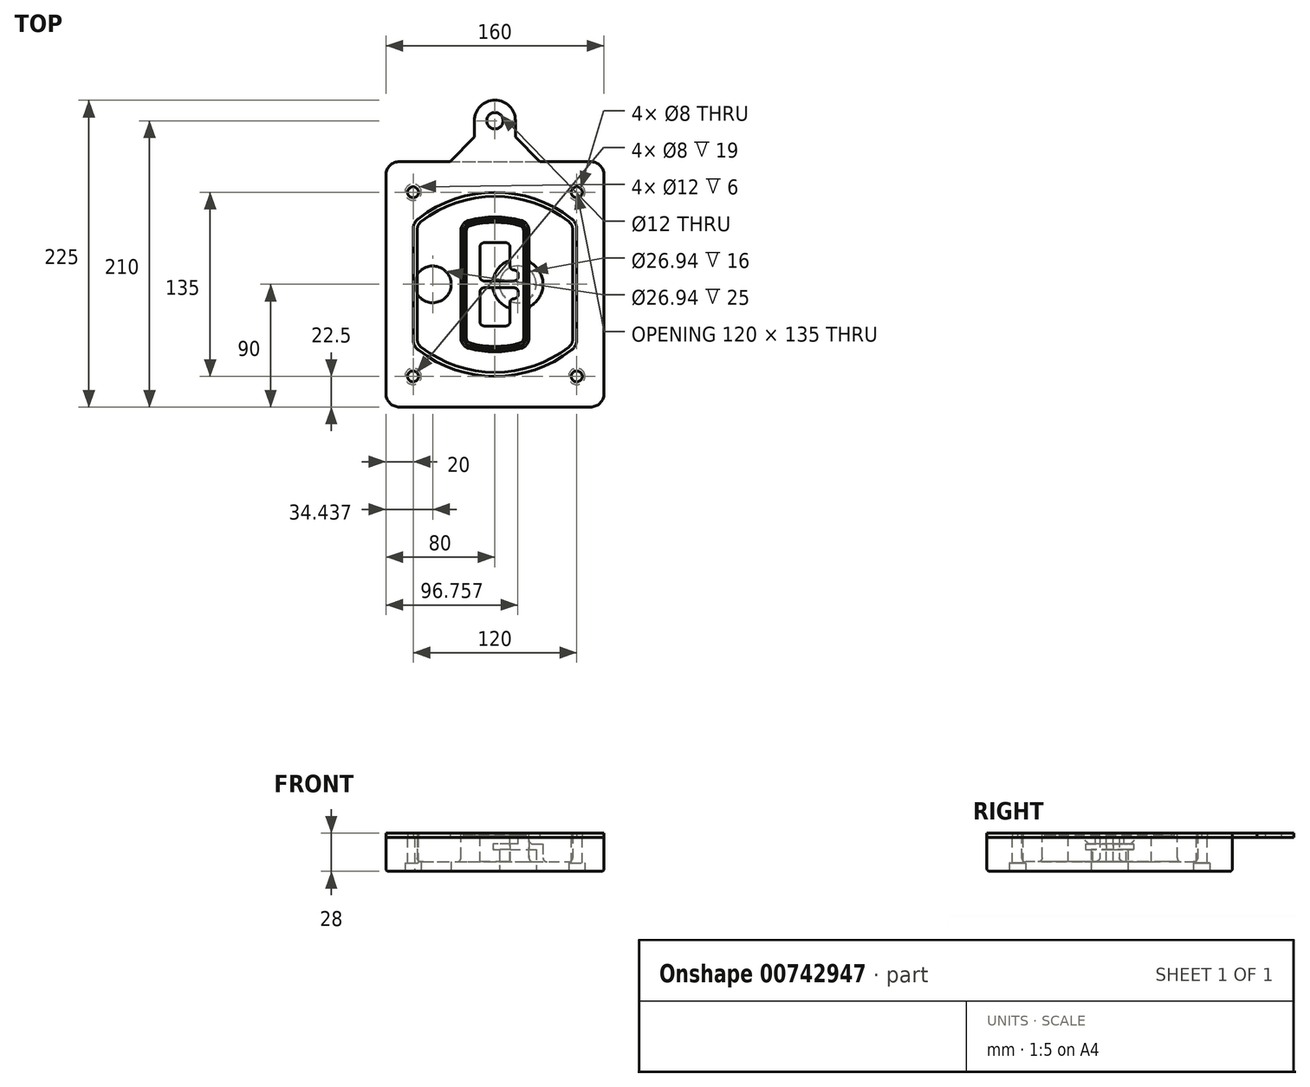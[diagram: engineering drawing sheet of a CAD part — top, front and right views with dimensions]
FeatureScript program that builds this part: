
annotation { "Feature Type Name" : "Feature", "Feature Type Description" : "" }
export const myFeature = defineFeature(function(context is Context, id is Id, definition is map)
    precondition{}
    {
        {
            var Q0;
            Q0=qCreatedBy(makeId("Top.planeOp"),FACE);
            var sketch = newSketch(context, id + "F0", { "sketchPlane" : qUnion([Q0])});
            skPoint(sketch, "E0.rect.middle", {"position": v(0, 0) * mm});
            skLineSegment(sketch, "E1.bottom", {"start": v(-70, -90) * mm, "end": v(70, -90) * mm});
            skLineSegment(sketch, "E1.top", {"start": v(-70, 90) * mm, "end": v(70, 90) * mm});
            skLineSegment(sketch, "E1.left", {"start": v(-80, -80) * mm, "end": v(-80, 80) * mm});
            skLineSegment(sketch, "E1.right", {"start": v(80, -80) * mm, "end": v(80, 80) * mm});
            skLineSegment(sketch, "E2", {"start": v(-80, 90) * mm, "end": v(80, -90) * mm, "construction": true});
            skLineSegment(sketch, "E3", {"start": v(80, 90) * mm, "end": v(-80, -90) * mm, "construction": true});
            skCircle(sketch, "E4", {"center": v(-60, 67.5) * mm, "radius": 4 * mm});
            skCircle(sketch, "E5", {"center": v(60, 67.5) * mm, "radius": 4 * mm});
            skCircle(sketch, "E6", {"center": v(60, -67.5) * mm, "radius": 4 * mm});
            skCircle(sketch, "E7", {"center": v(-60, -67.5) * mm, "radius": 4 * mm});
            skLineSegment(sketch, "E8", {"start": v(-60, 67.5) * mm, "end": v(60, 67.5) * mm, "construction": true});
            skLineSegment(sketch, "E9", {"start": v(60, 67.5) * mm, "end": v(60, -67.5) * mm, "construction": true});
            skLineSegment(sketch, "E10", {"start": v(60, -67.5) * mm, "end": v(-60, -67.5) * mm, "construction": true});
            skLineSegment(sketch, "E11", {"start": v(-60, -67.5) * mm, "end": v(-60, 67.5) * mm, "construction": true});
            skLineSegment(sketch, "E12", {"start": v(-60, 40.3) * mm, "end": v(-60, -40.3) * mm});
            skLineSegment(sketch, "E13", {"start": v(60, 40.3) * mm, "end": v(60, -40.3) * mm});
            skArc(sketch, "E14", {"start": v(56.15, 48.18) * mm, "mid": v(0, 67.5) * mm, "end": v(-56.15, 48.18) * mm});
            skArc(sketch, "E15", {"start": v(-56.15, -48.18) * mm, "mid": v(0, -67.5) * mm, "end": v(56.15, -48.18) * mm});
            skLineSegment(sketch, "E16", {"start": v(-60, 0) * mm, "end": v(60, 0) * mm, "construction": true});
            skPoint(sketch, "E17.visualSharp", {"position": v(-60, -45) * mm});
            skArc(sketch, "E17.filletArc", {"start": v(-60, -40.3) * mm, "mid": v(-58.99, -44.68) * mm, "end": v(-56.15, -48.18) * mm});
            skPoint(sketch, "E18.visualSharp", {"position": v(-60, 45) * mm});
            skArc(sketch, "E18.filletArc", {"start": v(-56.15, 48.18) * mm, "mid": v(-58.99, 44.68) * mm, "end": v(-60, 40.3) * mm});
            skPoint(sketch, "E19.visualSharp", {"position": v(60, 45) * mm});
            skArc(sketch, "E19.filletArc", {"start": v(60, 40.3) * mm, "mid": v(58.99, 44.68) * mm, "end": v(56.15, 48.18) * mm});
            skPoint(sketch, "E20.visualSharp", {"position": v(60, -45) * mm});
            skArc(sketch, "E20.filletArc", {"start": v(56.15, -48.18) * mm, "mid": v(58.99, -44.68) * mm, "end": v(60, -40.3) * mm});
            skPoint(sketch, "E21.visualSharp", {"position": v(-80, 90) * mm});
            skArc(sketch, "E21.filletArc", {"start": v(-70, 90) * mm, "mid": v(-77.07, 87.07) * mm, "end": v(-80, 80) * mm});
            skPoint(sketch, "E22.visualSharp", {"position": v(80, 90) * mm});
            skArc(sketch, "E22.filletArc", {"start": v(80, 80) * mm, "mid": v(77.07, 87.07) * mm, "end": v(70, 90) * mm});
            skPoint(sketch, "E23.visualSharp", {"position": v(80, -90) * mm});
            skArc(sketch, "E23.filletArc", {"start": v(70, -90) * mm, "mid": v(77.07, -87.07) * mm, "end": v(80, -80) * mm});
            skPoint(sketch, "E24.visualSharp", {"position": v(-80, -90) * mm});
            skArc(sketch, "E24.filletArc", {"start": v(-80, -80) * mm, "mid": v(-77.07, -87.07) * mm, "end": v(-70, -90) * mm});
            skArc(sketch, "E25.0", {"start": v(57, 40.3) * mm, "mid": v(56.3, 43.36) * mm, "end": v(54.3, 45.81) * mm});
            skLineSegment(sketch, "E25.1", {"start": v(57, 40.3) * mm, "end": v(57, -40.3) * mm});
            skArc(sketch, "E25.2", {"start": v(54.3, -45.81) * mm, "mid": v(56.3, -43.36) * mm, "end": v(57, -40.3) * mm});
            skArc(sketch, "E25.3", {"start": v(-54.3, -45.81) * mm, "mid": v(0, -64.5) * mm, "end": v(54.3, -45.81) * mm});
            skArc(sketch, "E25.4", {"start": v(-57, -40.3) * mm, "mid": v(-56.3, -43.36) * mm, "end": v(-54.3, -45.81) * mm});
            skArc(sketch, "E25.5", {"start": v(54.3, 45.81) * mm, "mid": v(0, 64.5) * mm, "end": v(-54.3, 45.81) * mm});
            skLineSegment(sketch, "E25.6", {"start": v(-57, 40.3) * mm, "end": v(-57, -40.3) * mm});
            skArc(sketch, "E25.7", {"start": v(-54.3, 45.81) * mm, "mid": v(-56.3, 43.36) * mm, "end": v(-57, 40.3) * mm});
            skArc(sketch, "E26.0", {"start": v(-58.62, 51.33) * mm, "mid": v(-62.58, 46.43) * mm, "end": v(-64, 40.3) * mm});
            skArc(sketch, "E26.1", {"start": v(58.62, 51.33) * mm, "mid": v(0, 71.5) * mm, "end": v(-58.62, 51.33) * mm});
            skArc(sketch, "E26.2", {"start": v(64, 40.3) * mm, "mid": v(62.58, 46.43) * mm, "end": v(58.62, 51.33) * mm});
            skLineSegment(sketch, "E26.3", {"start": v(64, 40.3) * mm, "end": v(64, -40.3) * mm});
            skArc(sketch, "E26.4", {"start": v(58.62, -51.33) * mm, "mid": v(62.58, -46.43) * mm, "end": v(64, -40.3) * mm});
            skLineSegment(sketch, "E26.5", {"start": v(-64, 40.3) * mm, "end": v(-64, -40.3) * mm});
            skArc(sketch, "E26.6", {"start": v(-58.62, -51.33) * mm, "mid": v(0, -71.5) * mm, "end": v(58.62, -51.33) * mm});
            skArc(sketch, "E26.7", {"start": v(-64, -40.3) * mm, "mid": v(-62.58, -46.43) * mm, "end": v(-58.62, -51.33) * mm});
            skSolve(sketch);
        }
        {
            var Q0;
            Q0=makeQuery(id+"F0.imprint","IMPRINT",FACE,{"disambiguationData":[TD([[makeQuery(id+"F0.imprint","IMPRINT",EDGE,{"derivedFrom":sQuery(id+"F0.wireOp",EDGE,"E1.bottom")}),1.0]])]});
            var Q1;
            Q1=makeQuery(id+"F0.imprint","IMPRINT",FACE,{"disambiguationData":[TD([[makeQuery(id+"F0.imprint","IMPRINT",EDGE,{"derivedFrom":sQuery(id+"F0.wireOp",EDGE,"E12")}),1.0]])]});
            var Q2;
            Q2=makeQuery(id+"F0.imprint","IMPRINT",FACE,{"disambiguationData":[TD([[makeQuery(id+"F0.imprint","IMPRINT",EDGE,{"derivedFrom":sQuery(id+"F0.wireOp",EDGE,"E25.0")}),1.0]])]});
            var Q3;
            Q3=makeQuery(id+"F0.imprint","IMPRINT",FACE,{"disambiguationData":[TD([[makeQuery(id+"F0.imprint","IMPRINT",EDGE,{"derivedFrom":sQuery(id+"F0.wireOp",EDGE,"E12")}),-1.0]])]});
            extrude(context, id + "F1", {"entities" : qUnion([Q0, Q1, Q2, Q3]), "oppositeDirection" : true, "depth" : 25 * mm});
        }
        {
            var Q0;
            Q0=makeQuery(id+"F0.imprint","IMPRINT",FACE,{"disambiguationData":[TD([[makeQuery(id+"F0.imprint","IMPRINT",EDGE,{"derivedFrom":sQuery(id+"F0.wireOp",EDGE,"E12")}),1.0]])]});
            extrude(context, id + "F2", {"entities" : qUnion([Q0]), "operationType" : NewBodyOperationType.ADD, "depth" : 3 * mm, "offsetDistance" : 25 * mm});
        }
        {
            var Q0;
            Q0=makeQuery(id+"F0.imprint","IMPRINT",FACE,{"disambiguationData":[TD([[makeQuery(id+"F0.imprint","IMPRINT",EDGE,{"derivedFrom":sQuery(id+"F0.wireOp",EDGE,"E25.0")}),1.0]])]});
            extrude(context, id + "F3", {"entities" : qUnion([Q0]), "operationType" : NewBodyOperationType.REMOVE, "oppositeDirection" : true, "depth" : 18 * mm});
        }
        {
            var Q0;
            Q0=makeQuery(id+"F2.opExtrude","CAP_FACE",FACE,{"disambiguationData":[OSD([sQuery(id+"F0.wireOp",EDGE,"E12"),sQuery(id+"F0.wireOp",EDGE,"E13"),sQuery(id+"F0.wireOp",EDGE,"E14"),sQuery(id+"F0.wireOp",EDGE,"E15"),sQuery(id+"F0.wireOp",EDGE,"E17.filletArc"),sQuery(id+"F0.wireOp",EDGE,"E18.filletArc"),sQuery(id+"F0.wireOp",EDGE,"E19.filletArc"),sQuery(id+"F0.wireOp",EDGE,"E20.filletArc"),sQuery(id+"F0.wireOp",EDGE,"E25.0"),sQuery(id+"F0.wireOp",EDGE,"E25.1"),sQuery(id+"F0.wireOp",EDGE,"E25.2"),sQuery(id+"F0.wireOp",EDGE,"E25.3"),sQuery(id+"F0.wireOp",EDGE,"E25.4"),sQuery(id+"F0.wireOp",EDGE,"E25.5"),sQuery(id+"F0.wireOp",EDGE,"E25.6"),sQuery(id+"F0.wireOp",EDGE,"E25.7")])],"isStart":false});
            var sketch = newSketch(context, id + "F4", { "sketchPlane" : qUnion([Q0])});
            skArc(sketch, "E27.0", {"start": v(-19.08, -46.97) * mm, "mid": v(0, -49.5) * mm, "end": v(19.08, -46.97) * mm});
            skArc(sketch, "E28.0", {"start": v(19.08, 46.97) * mm, "mid": v(0, 49.5) * mm, "end": v(-19.08, 46.97) * mm});
            skLineSegment(sketch, "E29", {"start": v(-25, 39.25) * mm, "end": v(-25, -39.25) * mm});
            skLineSegment(sketch, "E30", {"start": v(25, 39.25) * mm, "end": v(25, -39.25) * mm});
            skLineSegment(sketch, "E31", {"start": v(-25, 45.1) * mm, "end": v(25, 45.1) * mm, "construction": true});
            skLineSegment(sketch, "E32", {"start": v(-25, -45.1) * mm, "end": v(25, -45.1) * mm, "construction": true});
            skPoint(sketch, "E33.visualSharp", {"position": v(-25, 45.1) * mm});
            skArc(sketch, "E33.filletArc", {"start": v(-19.08, 46.97) * mm, "mid": v(-23.35, 44.11) * mm, "end": v(-25, 39.25) * mm});
            skPoint(sketch, "E34.visualSharp", {"position": v(25, 45.1) * mm});
            skArc(sketch, "E34.filletArc", {"start": v(25, 39.25) * mm, "mid": v(23.35, 44.11) * mm, "end": v(19.08, 46.97) * mm});
            skPoint(sketch, "E35.visualSharp", {"position": v(25, -45.1) * mm});
            skArc(sketch, "E35.filletArc", {"start": v(19.08, -46.97) * mm, "mid": v(23.35, -44.11) * mm, "end": v(25, -39.25) * mm});
            skPoint(sketch, "E36.visualSharp", {"position": v(-25, -45.1) * mm});
            skArc(sketch, "E36.filletArc", {"start": v(-25, -39.25) * mm, "mid": v(-23.35, -44.11) * mm, "end": v(-19.08, -46.97) * mm});
            skArc(sketch, "E37.0", {"start": v(54.3, 45.81) * mm, "mid": v(0, 64.5) * mm, "end": v(-54.3, 45.81) * mm});
            skArc(sketch, "E37.1", {"start": v(-54.3, 45.81) * mm, "mid": v(-56.3, 43.36) * mm, "end": v(-57, 40.3) * mm});
            skLineSegment(sketch, "E37.2", {"start": v(-57, 40.3) * mm, "end": v(-57, -40.3) * mm});
            skArc(sketch, "E37.3", {"start": v(-57, -40.3) * mm, "mid": v(-56.3, -43.36) * mm, "end": v(-54.3, -45.81) * mm});
            skArc(sketch, "E37.4", {"start": v(-54.3, -45.81) * mm, "mid": v(0, -64.5) * mm, "end": v(54.3, -45.81) * mm});
            skArc(sketch, "E37.5", {"start": v(54.3, -45.81) * mm, "mid": v(56.3, -43.36) * mm, "end": v(57, -40.3) * mm});
            skLineSegment(sketch, "E37.6", {"start": v(57, 40.3) * mm, "end": v(57, -40.3) * mm});
            skArc(sketch, "E37.7", {"start": v(57, 40.3) * mm, "mid": v(56.3, 43.36) * mm, "end": v(54.3, 45.81) * mm});
            skLineSegment(sketch, "E38.0", {"start": v(23, 39.25) * mm, "end": v(23, -39.25) * mm});
            skArc(sketch, "E38.1", {"start": v(18.56, -45.04) * mm, "mid": v(21.76, -42.9) * mm, "end": v(23, -39.25) * mm});
            skArc(sketch, "E38.2", {"start": v(-18.56, -45.04) * mm, "mid": v(0, -47.5) * mm, "end": v(18.56, -45.04) * mm});
            skArc(sketch, "E38.3", {"start": v(-23, -39.25) * mm, "mid": v(-21.76, -42.9) * mm, "end": v(-18.56, -45.04) * mm});
            skLineSegment(sketch, "E38.4", {"start": v(-23, 39.25) * mm, "end": v(-23, -39.25) * mm});
            skArc(sketch, "E38.5", {"start": v(23, 39.25) * mm, "mid": v(21.76, 42.9) * mm, "end": v(18.56, 45.04) * mm});
            skArc(sketch, "E38.6", {"start": v(-18.56, 45.04) * mm, "mid": v(-21.76, 42.9) * mm, "end": v(-23, 39.25) * mm});
            skArc(sketch, "E38.7", {"start": v(18.56, 45.04) * mm, "mid": v(0, 47.5) * mm, "end": v(-18.56, 45.04) * mm});
            skArc(sketch, "E39.0", {"start": v(21, 39.25) * mm, "mid": v(20.18, 41.68) * mm, "end": v(18.04, 43.1) * mm});
            skLineSegment(sketch, "E39.1", {"start": v(21, 39.25) * mm, "end": v(21, -39.25) * mm});
            skArc(sketch, "E39.2", {"start": v(18.04, -43.1) * mm, "mid": v(20.18, -41.68) * mm, "end": v(21, -39.25) * mm});
            skArc(sketch, "E39.3", {"start": v(-18.04, -43.1) * mm, "mid": v(0, -45.5) * mm, "end": v(18.04, -43.1) * mm});
            skArc(sketch, "E39.4", {"start": v(-21, -39.25) * mm, "mid": v(-20.18, -41.68) * mm, "end": v(-18.04, -43.1) * mm});
            skArc(sketch, "E39.5", {"start": v(18.04, 43.1) * mm, "mid": v(0, 45.5) * mm, "end": v(-18.04, 43.1) * mm});
            skLineSegment(sketch, "E39.6", {"start": v(-21, 39.25) * mm, "end": v(-21, -39.25) * mm});
            skArc(sketch, "E39.7", {"start": v(-18.04, 43.1) * mm, "mid": v(-20.18, 41.68) * mm, "end": v(-21, 39.25) * mm});
            skLineSegment(sketch, "E40", {"start": v(-25, 0) * mm, "end": v(25, 0) * mm, "construction": true});
            skLineSegment(sketch, "E41", {"start": v(-11, 5.5) * mm, "end": v(-11, 27.5) * mm});
            skLineSegment(sketch, "E42", {"start": v(-8, 30.5) * mm, "end": v(8, 30.5) * mm});
            skLineSegment(sketch, "E43", {"start": v(11, 27.5) * mm, "end": v(11, 13.5) * mm});
            skLineSegment(sketch, "E44", {"start": v(14, 10.5) * mm, "end": v(14, 10.5) * mm});
            skLineSegment(sketch, "E45", {"start": v(17, 7.5) * mm, "end": v(17, 5.5) * mm});
            skLineSegment(sketch, "E46", {"start": v(14, 2.5) * mm, "end": v(-8, 2.5) * mm});
            skPoint(sketch, "E47.visualSharp", {"position": v(-11, 30.5) * mm});
            skArc(sketch, "E47.filletArc", {"start": v(-8, 30.5) * mm, "mid": v(-10.12, 29.62) * mm, "end": v(-11, 27.5) * mm});
            skPoint(sketch, "E48.visualSharp", {"position": v(11, 30.5) * mm});
            skArc(sketch, "E48.filletArc", {"start": v(11, 27.5) * mm, "mid": v(10.12, 29.62) * mm, "end": v(8, 30.5) * mm});
            skPoint(sketch, "E49.visualSharp", {"position": v(11, 10.5) * mm});
            skArc(sketch, "E49.filletArc", {"start": v(11, 13.5) * mm, "mid": v(11.88, 11.38) * mm, "end": v(14, 10.5) * mm});
            skPoint(sketch, "E50.visualSharp", {"position": v(17, 10.5) * mm});
            skArc(sketch, "E50.filletArc", {"start": v(17, 7.5) * mm, "mid": v(16.12, 9.62) * mm, "end": v(14, 10.5) * mm});
            skPoint(sketch, "E51.visualSharp", {"position": v(17, 2.5) * mm});
            skArc(sketch, "E51.filletArc", {"start": v(14, 2.5) * mm, "mid": v(16.12, 3.38) * mm, "end": v(17, 5.5) * mm});
            skPoint(sketch, "E52.visualSharp", {"position": v(-11, 2.5) * mm});
            skArc(sketch, "E52.filletArc", {"start": v(-11, 5.5) * mm, "mid": v(-10.12, 3.38) * mm, "end": v(-8, 2.5) * mm});
            skLineSegment(sketch, "E53.0.MirrorCS", {"start": v(14, -2.5) * mm, "end": v(-8, -2.5) * mm});
            skArc(sketch, "E54.0.MirrorCS", {"start": v(-11, -5.5) * mm, "mid": v(-10.12, -3.38) * mm, "end": v(-8, -2.5) * mm});
            skLineSegment(sketch, "E55.0.MirrorCS", {"start": v(-11, -5.5) * mm, "end": v(-11, -27.5) * mm});
            skArc(sketch, "E56.0.MirrorCS", {"start": v(-8, -30.5) * mm, "mid": v(-10.12, -29.62) * mm, "end": v(-11, -27.5) * mm});
            skLineSegment(sketch, "E57.0.MirrorCS", {"start": v(-8, -30.5) * mm, "end": v(8, -30.5) * mm});
            skArc(sketch, "E58.0.MirrorCS", {"start": v(11, -27.5) * mm, "mid": v(10.12, -29.62) * mm, "end": v(8, -30.5) * mm});
            skLineSegment(sketch, "E59.0.MirrorCS", {"start": v(11, -27.5) * mm, "end": v(11, -13.5) * mm});
            skArc(sketch, "E60.0.MirrorCS", {"start": v(11, -13.5) * mm, "mid": v(11.88, -11.38) * mm, "end": v(14, -10.5) * mm});
            skArc(sketch, "E61.0.MirrorCS", {"start": v(17, -7.5) * mm, "mid": v(16.12, -9.62) * mm, "end": v(14, -10.5) * mm});
            skLineSegment(sketch, "E62.0.MirrorCS", {"start": v(17, -7.5) * mm, "end": v(17, -5.5) * mm});
            skArc(sketch, "E63.0.MirrorCS", {"start": v(14, -2.5) * mm, "mid": v(16.12, -3.38) * mm, "end": v(17, -5.5) * mm});
            skSolve(sketch);
        }
        {
            var Q0;
            Q0=makeQuery(id+"F4.imprint","IMPRINT",FACE,{"disambiguationData":[TD([[makeQuery(id+"F4.imprint","IMPRINT",EDGE,{"derivedFrom":sQuery(id+"F4.wireOp",EDGE,"E27.0")}),1.0]])]});
            var Q1;
            Q1=makeQuery(id+"F4.imprint","IMPRINT",FACE,{"disambiguationData":[TD([[makeQuery(id+"F4.imprint","IMPRINT",EDGE,{"derivedFrom":sQuery(id+"F4.wireOp",EDGE,"E38.0")}),-1.0]])]});
            var Q2;
            Q2=makeQuery(id+"F4.imprint","IMPRINT",FACE,{"disambiguationData":[TD([[makeQuery(id+"F4.imprint","IMPRINT",EDGE,{"derivedFrom":sQuery(id+"F4.wireOp",EDGE,"E39.0")}),1.0]])]});
            extrude(context, id + "F5", {"entities" : qUnion([Q0, Q1, Q2]), "operationType" : NewBodyOperationType.ADD, "endBound" : BoundingType.UP_TO_NEXT, "oppositeDirection" : true, "depth" : 25 * mm});
        }
        {
            var Q0;
            Q0=makeQuery(id+"F4.imprint","IMPRINT",FACE,{"disambiguationData":[TD([[makeQuery(id+"F4.imprint","IMPRINT",EDGE,{"derivedFrom":sQuery(id+"F4.wireOp",EDGE,"E38.0")}),-1.0]])]});
            extrude(context, id + "F6", {"entities" : qUnion([Q0]), "operationType" : NewBodyOperationType.REMOVE, "oppositeDirection" : true, "depth" : 2 * mm});
        }
        {
            var Q0;
            Q0=makeQuery(id+"F1.opExtrude","CAP_FACE",FACE,{"disambiguationData":[OSD([sQuery(id+"F0.wireOp",EDGE,"E1.bottom"),sQuery(id+"F0.wireOp",EDGE,"E1.top"),sQuery(id+"F0.wireOp",EDGE,"E1.left"),sQuery(id+"F0.wireOp",EDGE,"E1.right"),sQuery(id+"F0.wireOp",EDGE,"E4"),sQuery(id+"F0.wireOp",EDGE,"E5"),sQuery(id+"F0.wireOp",EDGE,"E6"),sQuery(id+"F0.wireOp",EDGE,"E7"),sQuery(id+"F0.wireOp",EDGE,"E21.filletArc"),sQuery(id+"F0.wireOp",EDGE,"E22.filletArc"),sQuery(id+"F0.wireOp",EDGE,"E23.filletArc"),sQuery(id+"F0.wireOp",EDGE,"E24.filletArc")])],"isStart":false});
            var sketch = newSketch(context, id + "F7", { "sketchPlane" : qUnion([Q0])});
            skCircle(sketch, "E64", {"center": v(16.76, 0) * mm, "radius": 13.47 * mm});
            skCircle(sketch, "E65", {"center": v(-45.56, 0) * mm, "radius": 13.47 * mm});
            skLineSegment(sketch, "E66", {"start": v(80, 0) * mm, "end": v(-80, 0) * mm});
            skCircle(sketch, "E67", {"center": v(16.76, 0) * mm, "radius": 18.47 * mm});
            skCircle(sketch, "E68", {"center": v(60, -67.5) * mm, "radius": 6 * mm});
            skCircle(sketch, "E69", {"center": v(-60, -67.5) * mm, "radius": 6 * mm});
            skCircle(sketch, "E70", {"center": v(-60, 67.5) * mm, "radius": 6 * mm});
            skCircle(sketch, "E71", {"center": v(60, 67.5) * mm, "radius": 6 * mm});
            skSolve(sketch);
        }
        {
            var Q0;
            {var subQ1=sQuery(id+"F7.wireOp",EDGE,"E66");var subQ4=sQuery(id+"F7.wireOp",EDGE,"E64");var subQ6=makeQuery(id+"F7.imprint","INTERSECT",VERTEX,{"disambiguationData":[OD(0.0)],"derivedFrom":[subQ4,subQ1]});Q0=makeQuery(id+"F7.imprint","IMPRINT",FACE,{"disambiguationData":[TD([[makeQuery(id+"F7.imprint","IMPRINT",EDGE,{"disambiguationData":[TD([[subQ6,-1.0]])],"derivedFrom":subQ4}),-1.0]])]});}
            var Q1;
            {var subQ0=sQuery(id+"F7.wireOp",EDGE,"E66");var subQ1=sQuery(id+"F7.wireOp",EDGE,"E64");var subQ3=makeQuery(id+"F7.imprint","INTERSECT",VERTEX,{"disambiguationData":[OD(0.0)],"derivedFrom":[subQ1,subQ0]});Q1=makeQuery(id+"F7.imprint","IMPRINT",FACE,{"disambiguationData":[TD([[makeQuery(id+"F7.imprint","IMPRINT",EDGE,{"disambiguationData":[TD([[subQ3,-1.0]])],"derivedFrom":subQ1}),1.0]])]});}
            var Q2;
            {var subQ0=sQuery(id+"F7.wireOp",EDGE,"E66");var subQ1=sQuery(id+"F7.wireOp",EDGE,"E64");var subQ3=makeQuery(id+"F7.imprint","INTERSECT",VERTEX,{"disambiguationData":[OD(0.0)],"derivedFrom":[subQ1,subQ0]});Q2=makeQuery(id+"F7.imprint","IMPRINT",FACE,{"disambiguationData":[TD([[makeQuery(id+"F7.imprint","IMPRINT",EDGE,{"disambiguationData":[TD([[subQ3,1.0]])],"derivedFrom":subQ1}),1.0]])]});}
            var Q3;
            {var subQ1=sQuery(id+"F7.wireOp",EDGE,"E66");var subQ4=sQuery(id+"F7.wireOp",EDGE,"E64");var subQ6=makeQuery(id+"F7.imprint","INTERSECT",VERTEX,{"disambiguationData":[OD(0.0)],"derivedFrom":[subQ4,subQ1]});Q3=makeQuery(id+"F7.imprint","IMPRINT",FACE,{"disambiguationData":[TD([[makeQuery(id+"F7.imprint","IMPRINT",EDGE,{"disambiguationData":[TD([[subQ6,1.0]])],"derivedFrom":subQ4}),-1.0]])]});}
            extrude(context, id + "F8", {"entities" : qUnion([Q0, Q1, Q2, Q3]), "operationType" : NewBodyOperationType.ADD, "oppositeDirection" : true, "depth" : 20 * mm});
        }
        {
            var Q0;
            {var subQ0=sQuery(id+"F7.wireOp",EDGE,"E66");var subQ1=sQuery(id+"F7.wireOp",EDGE,"E64");var subQ3=makeQuery(id+"F7.imprint","INTERSECT",VERTEX,{"disambiguationData":[OD(0.0)],"derivedFrom":[subQ1,subQ0]});Q0=makeQuery(id+"F7.imprint","IMPRINT",FACE,{"disambiguationData":[TD([[makeQuery(id+"F7.imprint","IMPRINT",EDGE,{"disambiguationData":[TD([[subQ3,-1.0]])],"derivedFrom":subQ1}),1.0]])]});}
            var Q1;
            {var subQ0=sQuery(id+"F7.wireOp",EDGE,"E66");var subQ1=sQuery(id+"F7.wireOp",EDGE,"E64");var subQ3=makeQuery(id+"F7.imprint","INTERSECT",VERTEX,{"disambiguationData":[OD(0.0)],"derivedFrom":[subQ1,subQ0]});Q1=makeQuery(id+"F7.imprint","IMPRINT",FACE,{"disambiguationData":[TD([[makeQuery(id+"F7.imprint","IMPRINT",EDGE,{"disambiguationData":[TD([[subQ3,1.0]])],"derivedFrom":subQ1}),1.0]])]});}
            extrude(context, id + "F9", {"entities" : qUnion([Q0, Q1]), "operationType" : NewBodyOperationType.REMOVE, "oppositeDirection" : true, "depth" : 16 * mm});
        }
        {
            var Q0;
            {var subQ0=sQuery(id+"F7.wireOp",EDGE,"E66");var subQ1=sQuery(id+"F7.wireOp",EDGE,"E65");var subQ3=makeQuery(id+"F7.imprint","INTERSECT",VERTEX,{"disambiguationData":[OD(0.0)],"derivedFrom":[subQ1,subQ0]});Q0=makeQuery(id+"F7.imprint","IMPRINT",FACE,{"disambiguationData":[TD([[makeQuery(id+"F7.imprint","IMPRINT",EDGE,{"disambiguationData":[TD([[subQ3,-1.0]])],"derivedFrom":subQ1}),1.0]])]});}
            var Q1;
            {var subQ0=sQuery(id+"F7.wireOp",EDGE,"E66");var subQ1=sQuery(id+"F7.wireOp",EDGE,"E65");var subQ3=makeQuery(id+"F7.imprint","INTERSECT",VERTEX,{"disambiguationData":[OD(0.0)],"derivedFrom":[subQ1,subQ0]});Q1=makeQuery(id+"F7.imprint","IMPRINT",FACE,{"disambiguationData":[TD([[makeQuery(id+"F7.imprint","IMPRINT",EDGE,{"disambiguationData":[TD([[subQ3,1.0]])],"derivedFrom":subQ1}),1.0]])]});}
            extrude(context, id + "F10", {"entities" : qUnion([Q0, Q1]), "operationType" : NewBodyOperationType.REMOVE, "oppositeDirection" : true, "depth" : 25 * mm});
        }
        {
            var Q0;
            Q0=makeQuery(id+"F7.imprint","IMPRINT",FACE,{"disambiguationData":[TD([[makeQuery(id+"F7.imprint","IMPRINT",EDGE,{"derivedFrom":sQuery(id+"F7.wireOp",EDGE,"E68")}),1.0]])]});
            var Q1;
            Q1=makeQuery(id+"F7.imprint","IMPRINT",FACE,{"disambiguationData":[TD([[makeQuery(id+"F7.imprint","IMPRINT",EDGE,{"derivedFrom":makeQuery(id+"F1.opExtrude","CAP_EDGE",EDGE,{"disambiguationData":[OSD([sQuery(id+"F0.wireOp",EDGE,"E5")])],"isStart":false})}),-1.0]])]});
            var Q2;
            Q2=makeQuery(id+"F7.imprint","IMPRINT",FACE,{"disambiguationData":[TD([[makeQuery(id+"F7.imprint","IMPRINT",EDGE,{"derivedFrom":sQuery(id+"F7.wireOp",EDGE,"E69")}),1.0]])]});
            var Q3;
            Q3=makeQuery(id+"F7.imprint","IMPRINT",FACE,{"disambiguationData":[TD([[makeQuery(id+"F7.imprint","IMPRINT",EDGE,{"derivedFrom":makeQuery(id+"F1.opExtrude","CAP_EDGE",EDGE,{"disambiguationData":[OSD([sQuery(id+"F0.wireOp",EDGE,"E4")])],"isStart":false})}),-1.0]])]});
            var Q4;
            Q4=makeQuery(id+"F7.imprint","IMPRINT",FACE,{"disambiguationData":[TD([[makeQuery(id+"F7.imprint","IMPRINT",EDGE,{"derivedFrom":sQuery(id+"F7.wireOp",EDGE,"E70")}),1.0]])]});
            var Q5;
            Q5=makeQuery(id+"F7.imprint","IMPRINT",FACE,{"disambiguationData":[TD([[makeQuery(id+"F7.imprint","IMPRINT",EDGE,{"derivedFrom":makeQuery(id+"F1.opExtrude","CAP_EDGE",EDGE,{"disambiguationData":[OSD([sQuery(id+"F0.wireOp",EDGE,"E7")])],"isStart":false})}),-1.0]])]});
            var Q6;
            Q6=makeQuery(id+"F7.imprint","IMPRINT",FACE,{"disambiguationData":[TD([[makeQuery(id+"F7.imprint","IMPRINT",EDGE,{"derivedFrom":sQuery(id+"F7.wireOp",EDGE,"E71")}),1.0]])]});
            var Q7;
            Q7=makeQuery(id+"F7.imprint","IMPRINT",FACE,{"disambiguationData":[TD([[makeQuery(id+"F7.imprint","IMPRINT",EDGE,{"derivedFrom":makeQuery(id+"F1.opExtrude","CAP_EDGE",EDGE,{"disambiguationData":[OSD([sQuery(id+"F0.wireOp",EDGE,"E6")])],"isStart":false})}),-1.0]])]});
            extrude(context, id + "F11", {"entities" : qUnion([Q0, Q1, Q2, Q3, Q4, Q5, Q6, Q7]), "operationType" : NewBodyOperationType.REMOVE, "oppositeDirection" : true, "depth" : 6 * mm});
        }
        {
            var Q0;
            Q0=makeQuery(id+"F9.boolean.opBoolean","COPY",FACE,{"derivedFrom":makeQuery(id+"F9.opExtrude","CAP_FACE",FACE,{"disambiguationData":[OSD([sQuery(id+"F7.wireOp",EDGE,"E64")])],"isStart":false})});
            var sketch = newSketch(context, id + "F12", { "sketchPlane" : qUnion([Q0])});
            skArc(sketch, "E72.0", {"start": v(11, 17.55) * mm, "mid": v(2.57, 11.82) * mm, "end": v(-1.54, 2.5) * mm});
            skArc(sketch, "E72.1", {"start": v(-1.54, -2.5) * mm, "mid": v(2.57, -11.82) * mm, "end": v(11, -17.55) * mm});
            skLineSegment(sketch, "E73", {"start": v(-1.54, -2.5) * mm, "end": v(14, -2.5) * mm});
            skLineSegment(sketch, "E74.0", {"start": v(14, 2.5) * mm, "end": v(-1.54, 2.5) * mm});
            skArc(sketch, "E74.1", {"start": v(14, 2.5) * mm, "mid": v(16.12, 3.38) * mm, "end": v(17, 5.5) * mm});
            skLineSegment(sketch, "E74.2", {"start": v(17, 7.5) * mm, "end": v(17, 5.5) * mm});
            skArc(sketch, "E74.3", {"start": v(17, 7.5) * mm, "mid": v(16.12, 9.62) * mm, "end": v(14, 10.5) * mm});
            skArc(sketch, "E74.4", {"start": v(11, 13.5) * mm, "mid": v(11.88, 11.38) * mm, "end": v(14, 10.5) * mm});
            skLineSegment(sketch, "E74.5", {"start": v(11, 17.55) * mm, "end": v(11, 13.5) * mm});
            skLineSegment(sketch, "E74.7", {"start": v(14, -2.5) * mm, "end": v(-1.54, -2.5) * mm});
            skArc(sketch, "E74.8", {"start": v(14, -2.5) * mm, "mid": v(16.12, -3.38) * mm, "end": v(17, -5.5) * mm});
            skLineSegment(sketch, "E74.9", {"start": v(17, -7.5) * mm, "end": v(17, -5.5) * mm});
            skArc(sketch, "E74.10", {"start": v(17, -7.5) * mm, "mid": v(16.12, -9.62) * mm, "end": v(14, -10.5) * mm});
            skArc(sketch, "E74.11", {"start": v(11, -13.5) * mm, "mid": v(11.88, -11.38) * mm, "end": v(14, -10.5) * mm});
            skLineSegment(sketch, "E74.12", {"start": v(11, -17.55) * mm, "end": v(11, -13.5) * mm});
            skPoint(sketch, "E75.orphan", {"position": v(11, -27.5) * mm});
            skPoint(sketch, "E76.orphan", {"position": v(-8, -2.5) * mm});
            skPoint(sketch, "E77.orphan", {"position": v(-8, 2.5) * mm});
            skPoint(sketch, "E78.orphan", {"position": v(11, 27.5) * mm});
            skSolve(sketch);
        }
        {
            var Q0;
            {var subQ7=sQuery(id+"F12.wireOp",EDGE,"E72.0");var subQ14=sQuery(id+"F12.wireOp",EDGE,"E72.1");var subQ16=sQuery(id+"F12.wireOp",EDGE,"E74.1");var subQ18=sQuery(id+"F12.wireOp",EDGE,"E74.8");Q0=qUnion([makeQuery(id+"F12.imprint","IMPRINT",FACE,{"disambiguationData":[TD([[makeQuery(id+"F12.imprint","IMPRINT",EDGE,{"derivedFrom":subQ7}),1.0]])]}),makeQuery(id+"F12.imprint","IMPRINT",FACE,{"disambiguationData":[TD([[makeQuery(id+"F12.imprint","IMPRINT",EDGE,{"derivedFrom":subQ14}),1.0]])]}),makeQuery(id+"F12.imprint","IMPRINT",FACE,{"disambiguationData":[TD([[makeQuery(id+"F12.imprint","IMPRINT",EDGE,{"derivedFrom":subQ16}),1.0]])]}),makeQuery(id+"F12.imprint","IMPRINT",FACE,{"disambiguationData":[TD([[makeQuery(id+"F12.imprint","IMPRINT",EDGE,{"derivedFrom":subQ18}),-1.0]])]})]);}
            var Q1;
            Q1=makeQuery(id+"F5.boolean.opBoolean","SPLIT",FACE,{"disambiguationData":[TD([makeQuery(id+"F5.opExtrude","SWEPT_FACE",FACE,{"disambiguationData":[OSD([sQuery(id+"F4.wireOp",EDGE,"E41")])]})])],"derivedFrom":makeQuery(id+"F3.boolean.opBoolean","COPY",FACE,{"derivedFrom":makeQuery(id+"F3.opExtrude","CAP_FACE",FACE,{"disambiguationData":[OSD([sQuery(id+"F0.wireOp",EDGE,"E25.0"),sQuery(id+"F0.wireOp",EDGE,"E25.1"),sQuery(id+"F0.wireOp",EDGE,"E25.2"),sQuery(id+"F0.wireOp",EDGE,"E25.3"),sQuery(id+"F0.wireOp",EDGE,"E25.4"),sQuery(id+"F0.wireOp",EDGE,"E25.5"),sQuery(id+"F0.wireOp",EDGE,"E25.6"),sQuery(id+"F0.wireOp",EDGE,"E25.7")])],"isStart":false})})});
            extrude(context, id + "F13", {"entities" : qUnion([Q0]), "operationType" : NewBodyOperationType.REMOVE, "endBound" : BoundingType.UP_TO_SURFACE, "endBoundEntityFace" : qUnion([Q1]), "depth" : 25 * mm});
        }
        {
            var Q0;
            Q0=makeQuery(id+"F3.boolean.opBoolean","COPY",EDGE,{"derivedFrom":makeQuery(id+"F3.opExtrude","CAP_EDGE",EDGE,{"disambiguationData":[OSD([sQuery(id+"F0.wireOp",EDGE,"E25.6")])],"isStart":false})});
            var Q1;
            Q1=makeQuery(id+"F8.boolean.opBoolean","INTERSECT",EDGE,{"derivedFrom":[makeQuery(id+"F5.opExtrude","SWEPT_FACE",FACE,{"disambiguationData":[OSD([sQuery(id+"F4.wireOp",EDGE,"E30")])]}),makeQuery(id+"F8.opExtrude","CAP_FACE",FACE,{"disambiguationData":[OSD([sQuery(id+"F7.wireOp",EDGE,"E67")])],"isStart":false})]});
            var Q2;
            Q2=makeQuery(id+"F8.boolean.opBoolean","INTERSECT",EDGE,{"disambiguationData":[OD(1.0)],"derivedFrom":[makeQuery(id+"F5.opExtrude","SWEPT_FACE",FACE,{"disambiguationData":[OSD([sQuery(id+"F4.wireOp",EDGE,"E30")])]}),makeQuery(id+"F8.opExtrude","SWEPT_FACE",FACE,{"disambiguationData":[OSD([sQuery(id+"F7.wireOp",EDGE,"E67")])]})]});
            var Q3;
            {var subQ0=sQuery(id+"F4.wireOp",EDGE,"E30");Q3=makeQuery(id+"F8.boolean.opBoolean","SPLIT",EDGE,{"disambiguationData":[TD([makeQuery(id+"F5.opExtrude","SWEPT_FACE",FACE,{"disambiguationData":[OSD([sQuery(id+"F4.wireOp",EDGE,"E35.filletArc")])]})])],"derivedFrom":makeQuery(id+"F5.opExtrude","CAP_EDGE",EDGE,{"disambiguationData":[OSD([subQ0])],"isStart":false})});}
            var Q4;
            {var subQ0=sQuery(id+"F0.wireOp",EDGE,"E25.7");var subQ1=sQuery(id+"F0.wireOp",EDGE,"E25.1");var subQ2=sQuery(id+"F0.wireOp",EDGE,"E25.6");var subQ3=sQuery(id+"F0.wireOp",EDGE,"E25.5");var subQ4=sQuery(id+"F0.wireOp",EDGE,"E25.4");var subQ5=sQuery(id+"F0.wireOp",EDGE,"E25.0");var subQ6=sQuery(id+"F0.wireOp",EDGE,"E25.2");var subQ7=sQuery(id+"F0.wireOp",EDGE,"E25.3");Q4=makeQuery(id+"F8.boolean.opBoolean","INTERSECT",EDGE,{"derivedFrom":[makeQuery(id+"F5.boolean.opBoolean","SPLIT",FACE,{"disambiguationData":[TD([makeQuery(id+"F2.opExtrude","SWEPT_FACE",FACE,{"disambiguationData":[OSD([subQ5])]})])],"derivedFrom":makeQuery(id+"F3.boolean.opBoolean","COPY",FACE,{"derivedFrom":makeQuery(id+"F3.opExtrude","CAP_FACE",FACE,{"disambiguationData":[OSD([subQ5,subQ1,subQ6,subQ7,subQ4,subQ3,subQ2,subQ0])],"isStart":false})})}),makeQuery(id+"F8.opExtrude","SWEPT_FACE",FACE,{"disambiguationData":[OSD([sQuery(id+"F7.wireOp",EDGE,"E67")])]})]});}
            var Q5;
            Q5=makeQuery(id+"F8.boolean.opBoolean","INTERSECT",EDGE,{"disambiguationData":[OD(0.0)],"derivedFrom":[makeQuery(id+"F5.opExtrude","SWEPT_FACE",FACE,{"disambiguationData":[OSD([sQuery(id+"F4.wireOp",EDGE,"E30")])]}),makeQuery(id+"F8.opExtrude","SWEPT_FACE",FACE,{"disambiguationData":[OSD([sQuery(id+"F7.wireOp",EDGE,"E67")])]})]});
            fillet(context, id + "F14", {"entities" : qUnion([Q0, Q1, Q2, Q3, Q4, Q5]), "radius" : 3 * mm, "tangentPropagation" : true, "allowEdgeOverflow" : false});
        }
        {
            var Q0;
            Q0=makeQuery(id+"F1.opExtrude","CAP_EDGE",EDGE,{"disambiguationData":[OSD([sQuery(id+"F0.wireOp",EDGE,"E1.bottom")])],"isStart":false});
            fillet(context, id + "F15", {"entities" : qUnion([Q0]), "radius" : 2 * mm, "tangentPropagation" : true, "allowEdgeOverflow" : false});
        }
        {
            var Q0;
            {var subQ0=sQuery(id+"F0.wireOp",EDGE,"E21.filletArc");var subQ1=sQuery(id+"F0.wireOp",EDGE,"E7");var subQ2=sQuery(id+"F0.wireOp",EDGE,"E6");var subQ3=sQuery(id+"F0.wireOp",EDGE,"E5");var subQ4=sQuery(id+"F0.wireOp",EDGE,"E4");var subQ5=sQuery(id+"F0.wireOp",EDGE,"E22.filletArc");var subQ6=sQuery(id+"F0.wireOp",EDGE,"E1.bottom");var subQ7=sQuery(id+"F0.wireOp",EDGE,"E1.right");var subQ8=sQuery(id+"F0.wireOp",EDGE,"E1.top");var subQ9=sQuery(id+"F0.wireOp",EDGE,"E1.left");var subQ10=sQuery(id+"F0.wireOp",EDGE,"E23.filletArc");var subQ11=sQuery(id+"F0.wireOp",EDGE,"E24.filletArc");Q0=makeQuery(id+"F2.boolean.opBoolean","SPLIT",FACE,{"disambiguationData":[TD([makeQuery(id+"F1.opExtrude","SWEPT_FACE",FACE,{"disambiguationData":[OSD([subQ6])]})])],"derivedFrom":makeQuery(id+"F1.opExtrude","CAP_FACE",FACE,{"disambiguationData":[OSD([subQ6,subQ8,subQ9,subQ7,subQ4,subQ3,subQ2,subQ1,subQ0,subQ5,subQ10,subQ11])],"isStart":true})});}
            var sketch = newSketch(context, id + "F16", { "sketchPlane" : qUnion([Q0])});
            skCircle(sketch, "E79", {"center": v(0, 120) * mm, "radius": 6 * mm});
            skLineSegment(sketch, "E80", {"start": v(-15, 108) * mm, "end": v(-15, 120) * mm});
            skLineSegment(sketch, "E81", {"start": v(15, 108) * mm, "end": v(15, 120) * mm});
            skArc(sketch, "E82", {"start": v(15, 120) * mm, "mid": v(0, 135) * mm, "end": v(-15, 120) * mm});
            skLineSegment(sketch, "E83.0", {"start": v(-70, 90) * mm, "end": v(70, 90) * mm});
            skCircle(sketch, "E83.1", {"center": v(60, 67.5) * mm, "radius": 4 * mm});
            skArc(sketch, "E83.2", {"start": v(80, 80) * mm, "mid": v(77.07, 87.07) * mm, "end": v(70, 90) * mm});
            skLineSegment(sketch, "E83.3", {"start": v(80, -80) * mm, "end": v(80, 80) * mm});
            skCircle(sketch, "E83.4", {"center": v(-60, 67.5) * mm, "radius": 4 * mm});
            skArc(sketch, "E83.5", {"start": v(-70, 90) * mm, "mid": v(-77.07, 87.07) * mm, "end": v(-80, 80) * mm});
            skLineSegment(sketch, "E83.6", {"start": v(-80, -80) * mm, "end": v(-80, 80) * mm, "construction": true});
            skArc(sketch, "E83.7", {"start": v(56.15, 48.18) * mm, "mid": v(0, 67.5) * mm, "end": v(-56.15, 48.18) * mm});
            skArc(sketch, "E83.8", {"start": v(-56.15, 48.18) * mm, "mid": v(-58.99, 44.68) * mm, "end": v(-60, 40.3) * mm});
            skLineSegment(sketch, "E83.9", {"start": v(-60, 40.3) * mm, "end": v(-60, -40.3) * mm});
            skArc(sketch, "E83.10", {"start": v(60, 40.3) * mm, "mid": v(58.99, 44.68) * mm, "end": v(56.15, 48.18) * mm});
            skLineSegment(sketch, "E83.11", {"start": v(60, 40.3) * mm, "end": v(60, -40.3) * mm});
            skArc(sketch, "E83.12", {"start": v(-60, -40.3) * mm, "mid": v(-58.99, -44.68) * mm, "end": v(-56.15, -48.18) * mm});
            skArc(sketch, "E83.13", {"start": v(-56.15, -48.18) * mm, "mid": v(0, -67.5) * mm, "end": v(56.15, -48.18) * mm});
            skArc(sketch, "E83.14", {"start": v(-80, -80) * mm, "mid": v(-77.07, -87.07) * mm, "end": v(-70, -90) * mm});
            skCircle(sketch, "E83.15", {"center": v(-60, -67.5) * mm, "radius": 4 * mm});
            skLineSegment(sketch, "E83.16", {"start": v(-70, -90) * mm, "end": v(70, -90) * mm});
            skArc(sketch, "E83.17", {"start": v(56.15, -48.18) * mm, "mid": v(58.99, -44.68) * mm, "end": v(60, -40.3) * mm});
            skCircle(sketch, "E83.18", {"center": v(60, -67.5) * mm, "radius": 4 * mm});
            skArc(sketch, "E83.19", {"start": v(70, -90) * mm, "mid": v(77.07, -87.07) * mm, "end": v(80, -80) * mm});
            skLineSegment(sketch, "E84", {"start": v(-15, 108) * mm, "end": v(-33, 90) * mm});
            skLineSegment(sketch, "E85", {"start": v(15, 108) * mm, "end": v(33, 90) * mm});
            skLineSegment(sketch, "E86", {"start": v(0, 120) * mm, "end": v(0, 90) * mm, "construction": true});
            skLineSegment(sketch, "E87", {"start": v(-80, 0) * mm, "end": v(80, 0) * mm, "construction": true});
            skLineSegment(sketch, "E88.MirrorCS", {"start": v(0, -120) * mm, "end": v(0, -90) * mm, "construction": true});
            skArc(sketch, "E89.MirrorCS", {"start": v(15, -120) * mm, "mid": v(0, -135) * mm, "end": v(-15, -120) * mm});
            skLineSegment(sketch, "E90.MirrorCS", {"start": v(15, -108) * mm, "end": v(33, -90) * mm});
            skLineSegment(sketch, "E91.MirrorCS", {"start": v(15, -108) * mm, "end": v(15, -120) * mm});
            skLineSegment(sketch, "E92.MirrorCS", {"start": v(-15, -108) * mm, "end": v(-15, -120) * mm});
            skLineSegment(sketch, "E93.MirrorCS", {"start": v(-15, -108) * mm, "end": v(-33, -90) * mm});
            skCircle(sketch, "E94.MirrorC", {"center": v(0, -120) * mm, "radius": 6 * mm});
            skSolve(sketch);
        }
        {
            var Q0;
            Q0=makeQuery(id+"F16.imprint","IMPRINT",FACE,{"disambiguationData":[TD([[makeQuery(id+"F16.imprint","IMPRINT",EDGE,{"derivedFrom":sQuery(id+"F16.wireOp",EDGE,"E79")}),-1.0]])]});
            var Q1;
            Q1=makeQuery(id+"F16.imprint","IMPRINT",FACE,{"disambiguationData":[TD([[makeQuery(id+"F16.imprint","IMPRINT",EDGE,{"derivedFrom":sQuery(id+"F16.wireOp",EDGE,"E83.1")}),-1.0]])]});
            var Q2;
            Q2=makeQuery(id+"F16.imprint","IMPRINT",FACE,{"disambiguationData":[TD([[makeQuery(id+"F16.imprint","IMPRINT",EDGE,{"derivedFrom":sQuery(id+"F16.wireOp",EDGE,"E89.MirrorCS")}),-1.0]])]});
            var Q3;
            Q3=makeQuery(id+"F2.opExtrude","CAP_FACE",FACE,{"disambiguationData":[OSD([sQuery(id+"F0.wireOp",EDGE,"E12"),sQuery(id+"F0.wireOp",EDGE,"E13"),sQuery(id+"F0.wireOp",EDGE,"E14"),sQuery(id+"F0.wireOp",EDGE,"E15"),sQuery(id+"F0.wireOp",EDGE,"E17.filletArc"),sQuery(id+"F0.wireOp",EDGE,"E18.filletArc"),sQuery(id+"F0.wireOp",EDGE,"E19.filletArc"),sQuery(id+"F0.wireOp",EDGE,"E20.filletArc"),sQuery(id+"F0.wireOp",EDGE,"E25.0"),sQuery(id+"F0.wireOp",EDGE,"E25.1"),sQuery(id+"F0.wireOp",EDGE,"E25.2"),sQuery(id+"F0.wireOp",EDGE,"E25.3"),sQuery(id+"F0.wireOp",EDGE,"E25.4"),sQuery(id+"F0.wireOp",EDGE,"E25.5"),sQuery(id+"F0.wireOp",EDGE,"E25.6"),sQuery(id+"F0.wireOp",EDGE,"E25.7")])],"isStart":false});
            extrude(context, id + "F17", {"entities" : qUnion([Q0, Q1, Q2]), "endBound" : BoundingType.UP_TO_SURFACE, "depth" : 25 * mm, "endBoundEntityFace" : qUnion([Q3]), "offsetDistance" : 25 * mm});
        }
    });
